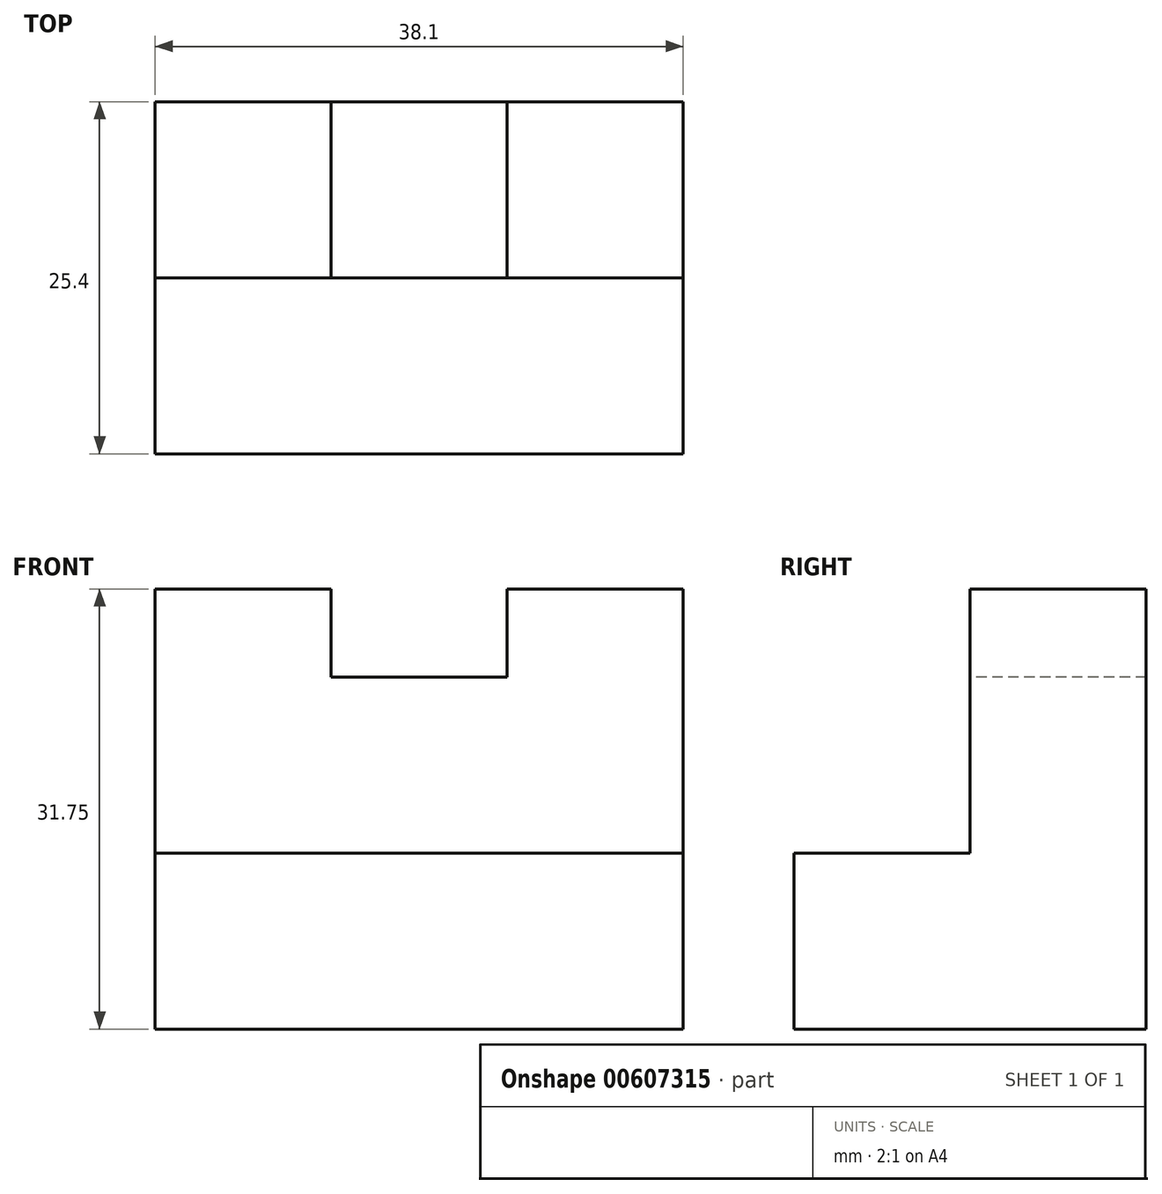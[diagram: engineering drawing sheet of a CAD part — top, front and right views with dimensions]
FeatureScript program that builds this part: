
annotation { "Feature Type Name" : "Feature", "Feature Type Description" : "" }
export const myFeature = defineFeature(function(context is Context, id is Id, definition is map)
    precondition{}
    {
        {
            var Q0;
            Q0=qCreatedBy(makeId("Right.planeOp"),FACE);
            var sketch = newSketch(context, id + "F0", { "sketchPlane" : qUnion([Q0])});
            skLineSegment(sketch, "E0", {"start": v(0, 0) * mm, "end": v(0, 31.75) * mm});
            skLineSegment(sketch, "E1", {"start": v(0, 31.75) * mm, "end": v(25.4, 31.75) * mm});
            skLineSegment(sketch, "E2", {"start": v(25.4, 31.75) * mm, "end": v(25.4, 0) * mm});
            skLineSegment(sketch, "E3", {"start": v(25.4, 0) * mm, "end": v(0, 0) * mm});
            skLineSegment(sketch, "E4", {"start": v(25.4, 31.75) * mm, "end": v(12.7, 31.75) * mm});
            skLineSegment(sketch, "E5", {"start": v(12.7, 31.75) * mm, "end": v(12.7, 12.7) * mm});
            skLineSegment(sketch, "E6", {"start": v(12.7, 12.7) * mm, "end": v(0, 12.7) * mm});
            skSolve(sketch);
        }
        {
            var Q0;
            Q0=makeQuery(id+"F0.imprint","IMPRINT",FACE,{"disambiguationData":[TD([[makeQuery(id+"F0.imprint","IMPRINT",EDGE,{"derivedFrom":sQuery(id+"F0.wireOp",EDGE,"E2")}),-1.0]])]});
            extrude(context, id + "F1", {"entities" : qUnion([Q0]), "depth" : 38.1 * mm, "offsetDistance" : 25.4 * mm});
        }
        {
            var Q0;
            Q0=makeQuery(id+"F1.opExtrude","SWEPT_FACE",FACE,{"disambiguationData":[OSD([sQuery(id+"F0.wireOp",EDGE,"E5")])]});
            var sketch = newSketch(context, id + "F2", { "sketchPlane" : qUnion([Q0])});
            skLineSegment(sketch, "E7", {"start": v(38.1, 31.75) * mm, "end": v(12.7, 31.75) * mm});
            skLineSegment(sketch, "E8", {"start": v(12.7, 31.75) * mm, "end": v(12.7, 25.4) * mm});
            skLineSegment(sketch, "E9", {"start": v(12.7, 25.4) * mm, "end": v(25.4, 25.4) * mm});
            skLineSegment(sketch, "E10", {"start": v(25.4, 25.4) * mm, "end": v(25.4, 31.75) * mm});
            skLineSegment(sketch, "E11", {"start": v(25.4, 31.75) * mm, "end": v(0, 31.75) * mm});
            skSolve(sketch);
        }
        {
            var Q0;
            {var subQ0=sQuery(id+"F2.wireOp",EDGE,"E8");Q0=makeQuery(id+"F2.imprint","IMPRINT",FACE,{"disambiguationData":[TD([[makeQuery(id+"F2.imprint","IMPRINT",EDGE,{"derivedFrom":subQ0}),1.0]])]});}
            extrude(context, id + "F3", {"entities" : qUnion([Q0]), "operationType" : NewBodyOperationType.REMOVE, "oppositeDirection" : true, "depth" : 12.7 * mm, "offsetDistance" : 25.4 * mm});
        }
    });
